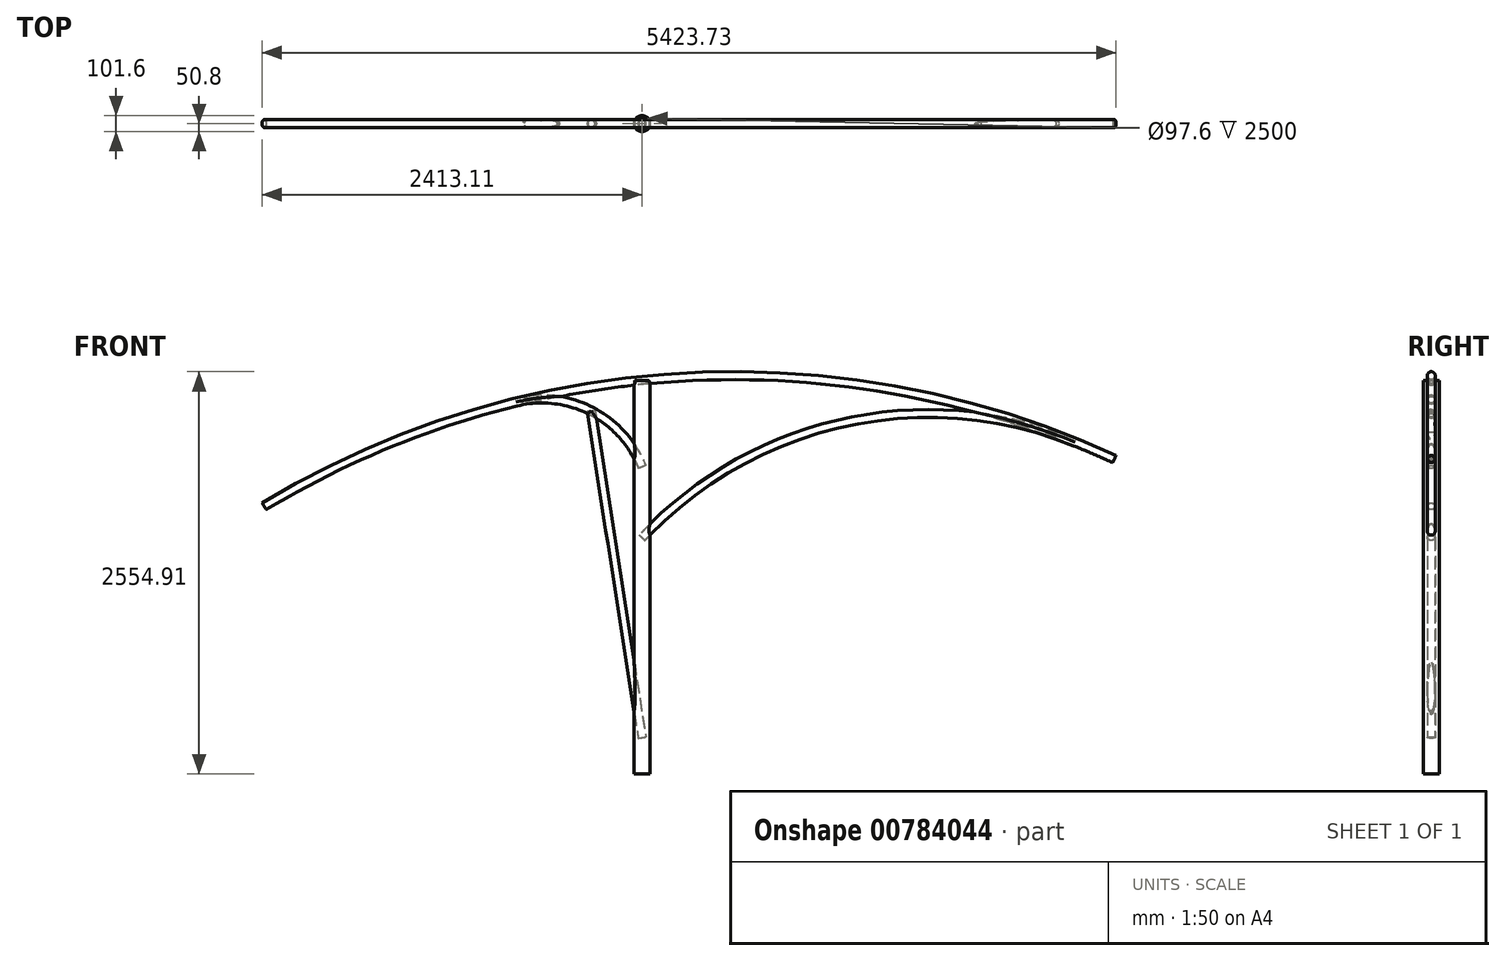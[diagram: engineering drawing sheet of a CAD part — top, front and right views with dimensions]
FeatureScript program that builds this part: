
annotation { "Feature Type Name" : "Feature", "Feature Type Description" : "" }
export const myFeature = defineFeature(function(context is Context, id is Id, definition is map)
    precondition{}
    {
        {
            var Q0;
            Q0=qCreatedBy(makeId("Right.planeOp"),FACE);
            var sketch = newSketch(context, id + "F0", { "sketchPlane" : qUnion([Q0])});
            skLineSegment(sketch, "E0", {"start": v(0, 0) * mm, "end": v(0, 2500) * mm});
            skSolve(sketch);
        }
        {
            var Q0;
            Q0=qCreatedBy(makeId("Front.planeOp"),FACE);
            var sketch = newSketch(context, id + "F1", { "sketchPlane" : qUnion([Q0])});
            skArc(sketch, "E1", {"start": v(3000, 2000) * mm, "mid": v(262.74, 2520.62) * mm, "end": v(-2400, 1700) * mm});
            skSolve(sketch);
        }
        {
            var Q0;
            Q0=qCreatedBy(makeId("Front.planeOp"),FACE);
            var sketch = newSketch(context, id + "F2", { "sketchPlane" : qUnion([Q0])});
            skArc(sketch, "E2", {"start": v(2750, 2108.02) * mm, "mid": v(1280.65, 2230.76) * mm, "end": v(0, 1500) * mm});
            skSolve(sketch);
        }
        {
            var Q0;
            Q0=qCreatedBy(makeId("Front.planeOp"),FACE);
            var sketch = newSketch(context, id + "F3", { "sketchPlane" : qUnion([Q0])});
            skArc(sketch, "E3", {"start": v(0, 1950) * mm, "mid": v(-322.93, 2305.6) * mm, "end": v(-800, 2361.52) * mm});
            skSolve(sketch);
        }
        {
            var Q0;
            Q0=qCreatedBy(makeId("Front.planeOp"),FACE);
            var sketch = newSketch(context, id + "F4", { "sketchPlane" : qUnion([Q0])});
            skLineSegment(sketch, "E4", {"start": v(0, 230.57) * mm, "end": v(-322.93, 2305.6) * mm});
            skSolve(sketch);
        }
        {
            var Q0;
            Q0=qCreatedBy(makeId("Top.planeOp"),FACE);
            var sketch = newSketch(context, id + "F5", { "sketchPlane" : qUnion([Q0])});
            skCircle(sketch, "E5", {"center": v(0, 0) * mm, "radius": 50.8 * mm});
            skCircle(sketch, "E6", {"center": v(0, 0) * mm, "radius": 48.8 * mm});
            skSolve(sketch);
        }
        {
            var Q0;
            Q0=makeQuery(id+"F5.imprint","IMPRINT",FACE,{"disambiguationData":[TD([[makeQuery(id+"F5.imprint","IMPRINT",EDGE,{"derivedFrom":sQuery(id+"F5.wireOp",EDGE,"E5")}),1.0]])]});
            var Q1;
            Q1=sQuery(id+"F0.wireOp",EDGE,"E0");
            sweep(context, id + "F6", {"profiles" : qUnion([Q0]), "path" : qUnion([Q1])});
        }
        {
            var Q0;
            Q0=sQuery(id+"F1.wireOp",VERTEX,"E1.start");
            var Q1;
            Q1=sQuery(id+"F1.wireOp",EDGE,"E1");
            cPlane(context, id + "F7", {"entities" : qUnion([Q0, Q1]), "cplaneType" : CPlaneType.CURVE_POINT, "offset" : 25 * mm, "width" : 150 * mm, "height" : 150 * mm});
        }
        {
            var Q0;
            Q0=qCreatedBy(id+"F7.planeOp",FACE);
            var sketch = newSketch(context, id + "F8", { "sketchPlane" : qUnion([Q0])});
            skCircle(sketch, "E7", {"center": v(0, 3071.2) * mm, "radius": 25.4 * mm});
            skCircle(sketch, "E8", {"center": v(0, 3071.2) * mm, "radius": 23.9 * mm});
            skSolve(sketch);
        }
        {
            var Q0;
            Q0=makeQuery(id+"F8.imprint","IMPRINT",FACE,{"disambiguationData":[TD([[makeQuery(id+"F8.imprint","IMPRINT",EDGE,{"derivedFrom":sQuery(id+"F8.wireOp",EDGE,"E7")}),1.0]])]});
            var Q1;
            Q1=sQuery(id+"F1.wireOp",EDGE,"E1");
            sweep(context, id + "F9", {"operationType" : NewBodyOperationType.ADD, "profiles" : qUnion([Q0]), "path" : qUnion([Q1])});
        }
        {
            var Q0;
            Q0=sQuery(id+"F2.wireOp",EDGE,"E2");
            var Q1;
            Q1=sQuery(id+"F2.wireOp",VERTEX,"E2.start");
            cPlane(context, id + "F10", {"entities" : qUnion([Q0, Q1]), "cplaneType" : CPlaneType.CURVE_POINT, "offset" : 25 * mm, "width" : 150 * mm, "height" : 150 * mm});
        }
        {
            var Q0;
            Q0=qCreatedBy(id+"F10.planeOp",FACE);
            var sketch = newSketch(context, id + "F11", { "sketchPlane" : qUnion([Q0])});
            skCircle(sketch, "E9", {"center": v(0, 2985.22) * mm, "radius": 25.4 * mm});
            skCircle(sketch, "E10", {"center": v(0, 2985.22) * mm, "radius": 23.9 * mm});
            skSolve(sketch);
        }
        {
            var Q0;
            Q0=makeQuery(id+"F11.imprint","IMPRINT",FACE,{"disambiguationData":[TD([[makeQuery(id+"F11.imprint","IMPRINT",EDGE,{"derivedFrom":sQuery(id+"F11.wireOp",EDGE,"E9")}),1.0]])]});
            var Q1;
            Q1=sQuery(id+"F2.wireOp",EDGE,"E2");
            sweep(context, id + "F12", {"operationType" : NewBodyOperationType.ADD, "profiles" : qUnion([Q0]), "path" : qUnion([Q1])});
        }
        {
            var Q0;
            Q0=sQuery(id+"F3.wireOp",EDGE,"E3");
            var Q1;
            Q1=sQuery(id+"F3.wireOp",VERTEX,"E3.end");
            cPlane(context, id + "F13", {"entities" : qUnion([Q0, Q1]), "cplaneType" : CPlaneType.CURVE_POINT, "offset" : 25 * mm, "width" : 150 * mm, "height" : 150 * mm});
        }
        {
            var Q0;
            Q0=qCreatedBy(id+"F13.planeOp",FACE);
            var sketch = newSketch(context, id + "F14", { "sketchPlane" : qUnion([Q0])});
            skCircle(sketch, "E11", {"center": v(0, 2484.36) * mm, "radius": 25.4 * mm});
            skCircle(sketch, "E12", {"center": v(0, 2484.36) * mm, "radius": 23.9 * mm});
            skSolve(sketch);
        }
        {
            var Q0;
            Q0=makeQuery(id+"F14.imprint","IMPRINT",FACE,{"disambiguationData":[TD([[makeQuery(id+"F14.imprint","IMPRINT",EDGE,{"derivedFrom":sQuery(id+"F14.wireOp",EDGE,"E11")}),1.0]])]});
            var Q1;
            Q1=sQuery(id+"F3.wireOp",EDGE,"E3");
            sweep(context, id + "F15", {"operationType" : NewBodyOperationType.ADD, "profiles" : qUnion([Q0]), "path" : qUnion([Q1])});
        }
        {
            var Q0;
            Q0=sQuery(id+"F4.wireOp",EDGE,"E4");
            var Q1;
            Q1=sQuery(id+"F4.wireOp",VERTEX,"E4.end");
            cPlane(context, id + "F16", {"entities" : qUnion([Q0, Q1]), "cplaneType" : CPlaneType.CURVE_POINT, "offset" : 25 * mm, "width" : 150 * mm, "height" : 150 * mm});
        }
        {
            var Q0;
            Q0=qCreatedBy(id+"F16.planeOp",FACE);
            var sketch = newSketch(context, id + "F17", { "sketchPlane" : qUnion([Q0])});
            skCircle(sketch, "E13", {"center": v(35.46, 0) * mm, "radius": 25.4 * mm});
            skCircle(sketch, "E14", {"center": v(35.46, 0) * mm, "radius": 23.9 * mm});
            skSolve(sketch);
        }
        {
            var Q0;
            Q0 = qSketchRegion(id + "F17", true);
            var Q1;
            Q1=sQuery(id+"F4.wireOp",EDGE,"E4");
            sweep(context, id + "F18", {"operationType" : NewBodyOperationType.ADD, "profiles" : qUnion([Q0]), "path" : qUnion([Q1])});
        }
    });
